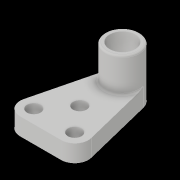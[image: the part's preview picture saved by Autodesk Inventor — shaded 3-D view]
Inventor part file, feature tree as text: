
AUTODESK INVENTOR PART (.ipt)
format: ipt  version: 2019 (Build 230136000, 136)  size: 135,168 bytes
history: native  units: mm
features: sketch x4, extrude x3, hole x1, fillet x1
ambient origin geometry x8: Origin, YZ Plane, XZ Plane, XY Plane, X Axis, Y Axis, Z Axis, Center Point
bodies: Solid1 (feature_tree)
feature tree (9):
  extrude  "Extrusion1"  Depth=24.0mm
  extrude  "Extrusion2"  Depth=10.0mm
  extrude  "Extrusion3"  Depth=10.0mm TaperAngle=0.0deg
  hole  "Hole1"  [1 undecoded]
  fillet  "Fillet1"  Radius=15.0mm
  sketch  "Sketch1"  dims[d0=8.0mm d1=24.0mm]
  sketch  "Sketch2"  dims[d2=10.0mm d3=40.0mm]
  sketch  "Sketch3"  dims[d4=10.0mm d5=0.0mm d6=20.0mm d7=0.0mm]
  sketch  "Sketch4"  dims[d8=15.0mm d9=20.0mm d10=0.0mm d11=15.0mm d12=12.0mm d13=8.0mm d14=6.0mm d15=12.0mm d16=3.0mm d17=90.0deg d18=8.0mm d19=20.594885mm d20=1.0mm]
note: 1 required parameter value undecoded (feature->parameter linkage not recoverable at this tier; creation-order binding heuristic only, values carry confidence <= 0.55)
